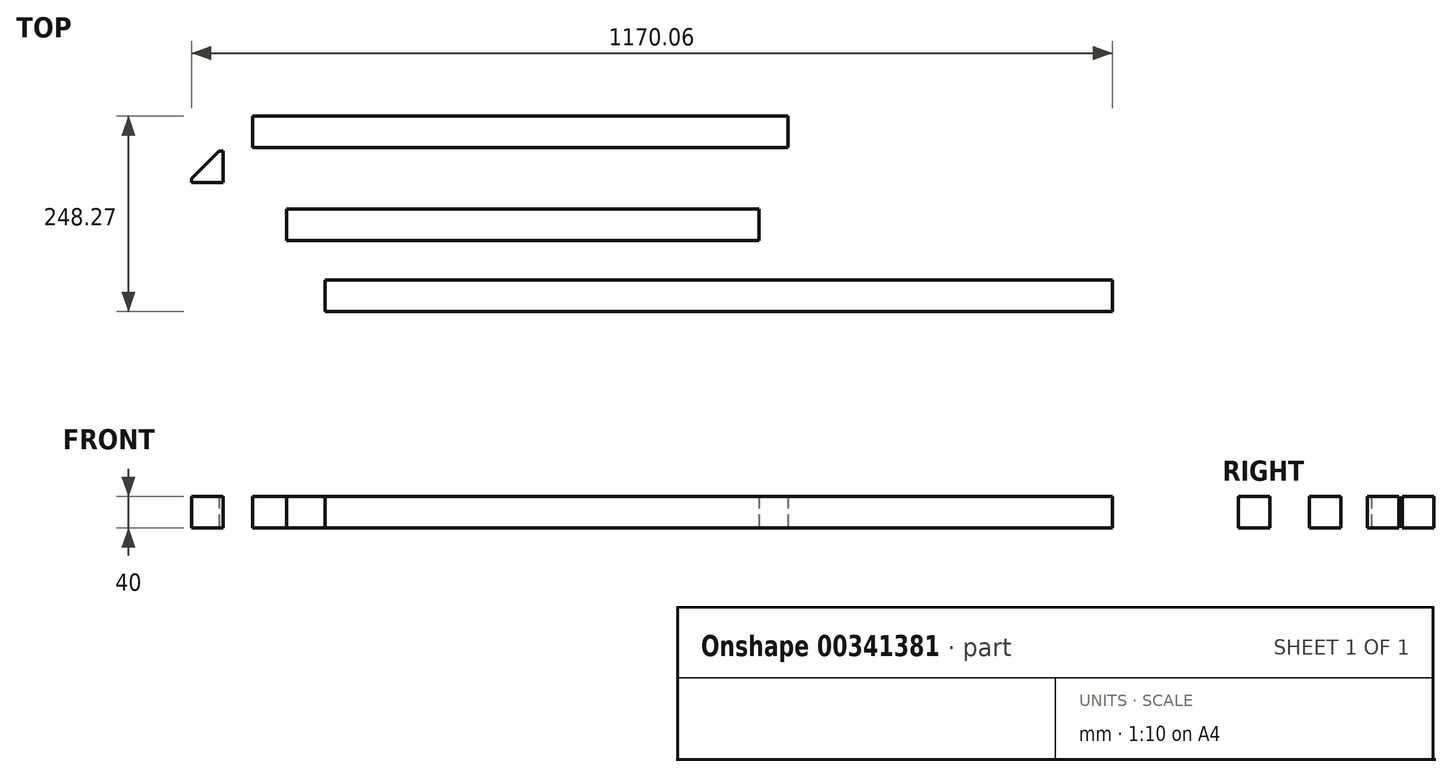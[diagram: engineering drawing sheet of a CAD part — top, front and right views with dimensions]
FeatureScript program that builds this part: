
annotation { "Feature Type Name" : "Feature", "Feature Type Description" : "" }
export const myFeature = defineFeature(function(context is Context, id is Id, definition is map)
    precondition{}
    {
        {
            var Q0;
            Q0=qCreatedBy(makeId("Top.planeOp"),FACE);
            var sketch = newSketch(context, id + "F0", { "sketchPlane" : qUnion([Q0])});
            skLineSegment(sketch, "E0.bottom", {"start": v(-215.92, 33.66) * mm, "end": v(384.08, 33.66) * mm});
            skLineSegment(sketch, "E0.top", {"start": v(-215.92, -6.34) * mm, "end": v(384.08, -6.34) * mm});
            skLineSegment(sketch, "E0.left", {"start": v(-215.92, 33.66) * mm, "end": v(-215.92, -6.34) * mm});
            skLineSegment(sketch, "E0.right", {"start": v(384.08, 33.66) * mm, "end": v(384.08, -6.34) * mm});
            skSolve(sketch);
        }
        {
            var Q0;
            Q0=makeQuery(id+"F0.imprint","IMPRINT",FACE,{"disambiguationData":[TD([[makeQuery(id+"F0.imprint","IMPRINT",EDGE,{"derivedFrom":sQuery(id+"F0.wireOp",EDGE,"E0.bottom")}),-1.0]])]});
            extrude(context, id + "F1", {"entities" : qUnion([Q0]), "depth" : 40 * mm});
        }
        {
            var Q0;
            Q0=qCreatedBy(makeId("Top.planeOp"),FACE);
            var sketch = newSketch(context, id + "F2", { "sketchPlane" : qUnion([Q0])});
            skLineSegment(sketch, "E1.bottom", {"start": v(-166.53, -56.24) * mm, "end": v(833.47, -56.24) * mm});
            skLineSegment(sketch, "E1.top", {"start": v(-166.53, -96.24) * mm, "end": v(833.47, -96.24) * mm});
            skLineSegment(sketch, "E1.left", {"start": v(-166.53, -56.24) * mm, "end": v(-166.53, -96.24) * mm});
            skLineSegment(sketch, "E1.right", {"start": v(833.47, -56.24) * mm, "end": v(833.47, -96.24) * mm});
            skSolve(sketch);
        }
        {
            var Q0;
            Q0=makeQuery(id+"F2.imprint","IMPRINT",FACE,{"disambiguationData":[TD([[makeQuery(id+"F2.imprint","IMPRINT",EDGE,{"derivedFrom":sQuery(id+"F2.wireOp",EDGE,"E1.bottom")}),-1.0]])]});
            extrude(context, id + "F3", {"entities" : qUnion([Q0]), "depth" : 40 * mm});
        }
        {
            var Q0;
            Q0=qCreatedBy(makeId("Top.planeOp"),FACE);
            var sketch = newSketch(context, id + "F4", { "sketchPlane" : qUnion([Q0])});
            skLineSegment(sketch, "E2", {"start": v(-336.59, 67.3) * mm, "end": v(-296.59, 67.3) * mm});
            skLineSegment(sketch, "E3", {"start": v(-296.59, 67.3) * mm, "end": v(-296.59, 107.3) * mm});
            skLineSegment(sketch, "E4", {"start": v(-296.59, 107.3) * mm, "end": v(-336.59, 67.3) * mm});
            skLineSegment(sketch, "E5", {"start": v(-336.59, 67.3) * mm, "end": v(-336.59, 72.3) * mm});
            skLineSegment(sketch, "E6", {"start": v(-336.59, 72.3) * mm, "end": v(-301.59, 107.3) * mm});
            skLineSegment(sketch, "E7", {"start": v(-301.59, 107.3) * mm, "end": v(-296.59, 107.3) * mm});
            skSolve(sketch);
        }
        {
            var Q0;
            Q0=makeQuery(id+"F4.imprint","IMPRINT",FACE,{"disambiguationData":[TD([[makeQuery(id+"F4.imprint","IMPRINT",EDGE,{"derivedFrom":sQuery(id+"F4.wireOp",EDGE,"E2")}),1.0]])]});
            var Q1;
            Q1=makeQuery(id+"F4.imprint","IMPRINT",FACE,{"disambiguationData":[TD([[makeQuery(id+"F4.imprint","IMPRINT",EDGE,{"derivedFrom":sQuery(id+"F4.wireOp",EDGE,"E4")}),-1.0]])]});
            extrude(context, id + "F5", {"entities" : qUnion([Q0, Q1]), "depth" : 40 * mm});
        }
        {
            var Q0;
            Q0=qCreatedBy(makeId("Top.planeOp"),FACE);
            var sketch = newSketch(context, id + "F6", { "sketchPlane" : qUnion([Q0])});
            skLineSegment(sketch, "E8.bottom", {"start": v(-259.12, 152.03) * mm, "end": v(420.88, 152.03) * mm});
            skLineSegment(sketch, "E8.top", {"start": v(-259.12, 112.03) * mm, "end": v(420.88, 112.03) * mm});
            skLineSegment(sketch, "E8.left", {"start": v(-259.12, 152.03) * mm, "end": v(-259.12, 112.03) * mm});
            skLineSegment(sketch, "E8.right", {"start": v(420.88, 152.03) * mm, "end": v(420.88, 112.03) * mm});
            skSolve(sketch);
        }
        {
            var Q0;
            Q0=makeQuery(id+"F6.imprint","IMPRINT",FACE,{"disambiguationData":[TD([[makeQuery(id+"F6.imprint","IMPRINT",EDGE,{"derivedFrom":sQuery(id+"F6.wireOp",EDGE,"E8.bottom")}),-1.0]])]});
            extrude(context, id + "F7", {"entities" : qUnion([Q0]), "depth" : 40 * mm});
        }
    });
